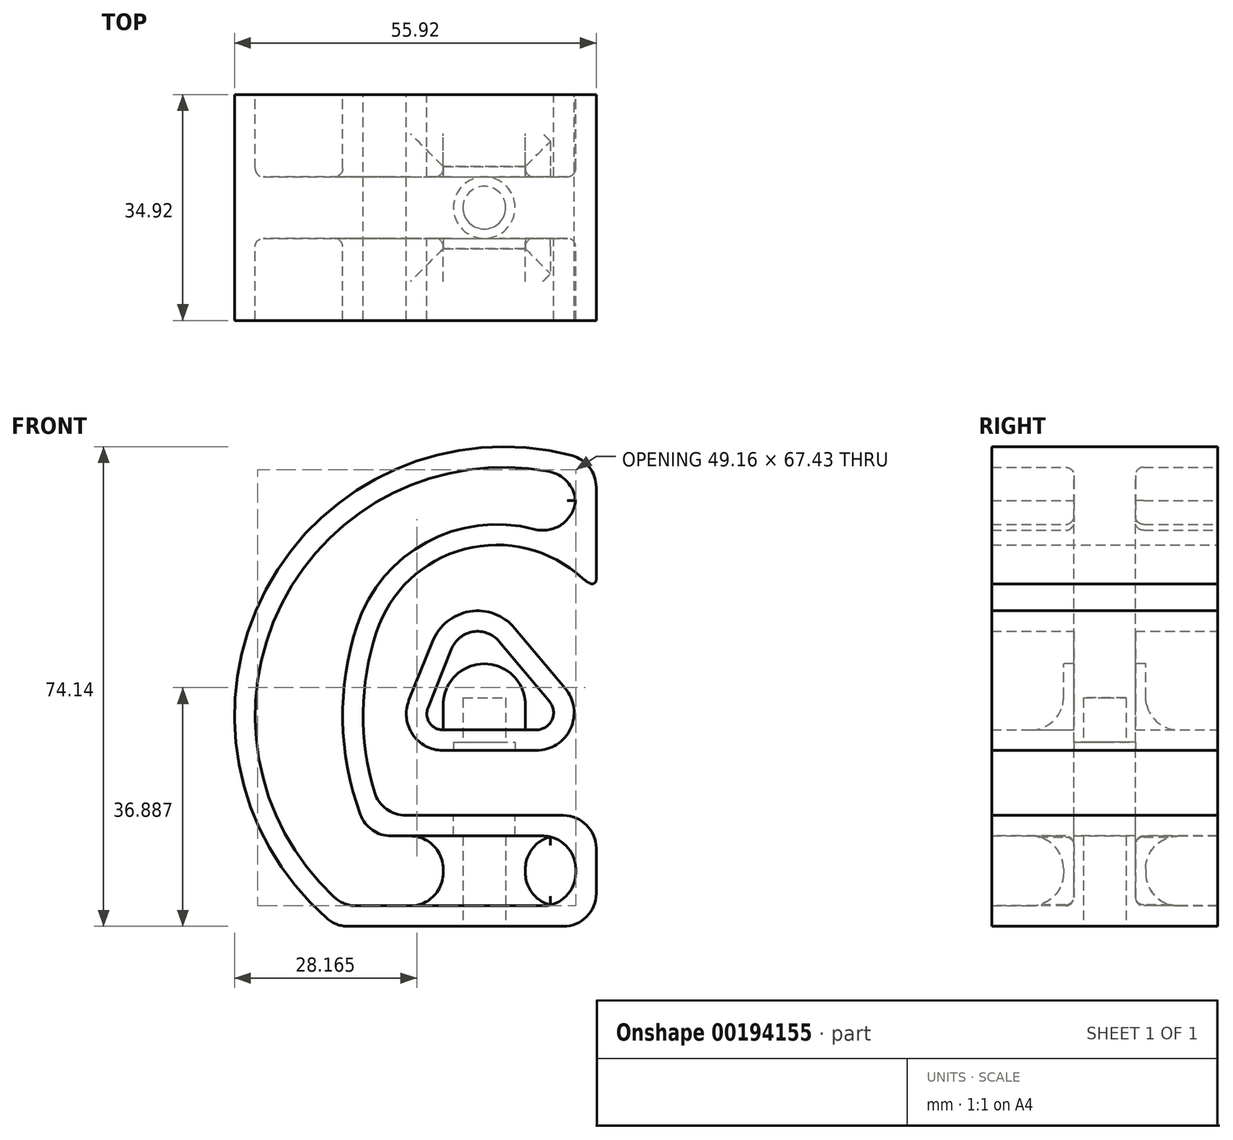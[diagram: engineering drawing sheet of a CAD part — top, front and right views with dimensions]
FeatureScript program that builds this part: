
annotation { "Feature Type Name" : "Feature", "Feature Type Description" : "" }
export const myFeature = defineFeature(function(context is Context, id is Id, definition is map)
    precondition{}
    {
        {
            var Q0;
            Q0=qCreatedBy(makeId("Front.planeOp"),FACE);
            var sketch = newSketch(context, id + "F0", { "sketchPlane" : qUnion([Q0])});
            skLineSegment(sketch, "E0", {"start": v(244.88, -10.5) * mm, "end": v(230.41, -10.5) * mm});
            skLineSegment(sketch, "E1", {"start": v(225.18, -2.77) * mm, "end": v(228.83, 6.36) * mm});
            skLineSegment(sketch, "E2", {"start": v(241.53, 8.4) * mm, "end": v(249.35, -0.9) * mm});
            skPoint(sketch, "E3.visualSharp", {"position": v(249.43, -10.5) * mm});
            skArc(sketch, "E3.filletArc", {"start": v(244.88, -10.5) * mm, "mid": v(250.17, -7.12) * mm, "end": v(249.35, -0.9) * mm});
            skArc(sketch, "E4", {"start": v(241.53, 8.4) * mm, "mid": v(234.6, 10.98) * mm, "end": v(228.83, 6.36) * mm});
            skArc(sketch, "E5", {"start": v(225.18, -2.77) * mm, "mid": v(225.74, -8.02) * mm, "end": v(230.41, -10.5) * mm});
            skPoint(sketch, "E6.visualSharp", {"position": v(249.72, -1.34) * mm});
            skLineSegment(sketch, "E7", {"start": v(254.14, 33.9) * mm, "end": v(254.14, 14.98) * mm});
            skLineSegment(sketch, "E8", {"start": v(254.14, 14.98) * mm, "end": v(253.16, 14.98) * mm});
            skLineSegment(sketch, "E9", {"start": v(213.99, -37.7) * mm, "end": v(254.14, -37.7) * mm});
            skLineSegment(sketch, "E10", {"start": v(254.14, -37.7) * mm, "end": v(254.14, -20.55) * mm});
            skLineSegment(sketch, "E11", {"start": v(254.14, -20.55) * mm, "end": v(221.13, -20.55) * mm});
            skArc(sketch, "E12", {"start": v(220.15, 7.77) * mm, "mid": v(218.13, -6.48) * mm, "end": v(221.13, -20.55) * mm});
            skArc(sketch, "E13", {"start": v(254.14, 33.9) * mm, "mid": v(203.53, 15.22) * mm, "end": v(213.99, -37.7) * mm});
            skArc(sketch, "E14", {"start": v(253.16, 14.98) * mm, "mid": v(234.6, 20.81) * mm, "end": v(220.15, 7.77) * mm});
            skLineSegment(sketch, "E15.0", {"start": v(239.1, 6.36) * mm, "end": v(246.92, -2.94) * mm});
            skLineSegment(sketch, "E15.1", {"start": v(228.13, -3.95) * mm, "end": v(231.78, 5.18) * mm});
            skArc(sketch, "E15.2", {"start": v(228.13, -3.95) * mm, "mid": v(228.37, -6.24) * mm, "end": v(230.41, -7.32) * mm});
            skArc(sketch, "E15.3", {"start": v(239.1, 6.36) * mm, "mid": v(235.1, 7.85) * mm, "end": v(231.78, 5.18) * mm});
            skLineSegment(sketch, "E15.4", {"start": v(244.88, -7.32) * mm, "end": v(230.41, -7.32) * mm});
            skArc(sketch, "E15.5", {"start": v(244.88, -7.32) * mm, "mid": v(247.3, -5.78) * mm, "end": v(246.92, -2.94) * mm});
            skLineSegment(sketch, "E16.0", {"start": v(250.96, 31.6) * mm, "end": v(250.96, 20.9) * mm});
            skArc(sketch, "E16.2", {"start": v(250.96, 31.6) * mm, "mid": v(206.04, 13.18) * mm, "end": v(215.12, -34.52) * mm});
            skArc(sketch, "E16.4", {"start": v(250.96, 20.9) * mm, "mid": v(231.08, 23.1) * mm, "end": v(217.13, 8.76) * mm});
            skLineSegment(sketch, "E16.5", {"start": v(215.12, -34.52) * mm, "end": v(250.96, -34.52) * mm});
            skLineSegment(sketch, "E16.6", {"start": v(250.96, -34.52) * mm, "end": v(250.96, -23.72) * mm});
            skLineSegment(sketch, "E16.7", {"start": v(250.96, -23.72) * mm, "end": v(219.05, -23.72) * mm});
            skArc(sketch, "E16.8", {"start": v(217.13, 8.76) * mm, "mid": v(215, -7.67) * mm, "end": v(219.05, -23.72) * mm});
            skSolve(sketch);
        }
        {
            var Q0;
            Q0 = qSketchRegion(id + "F0", true);
            extrude(context, id + "F1", {"entities" : qUnion([Q0]), "depth" : 34.92 * mm});
        }
        {
            var Q0;
            Q0=makeQuery(id+"F1.opExtrude","SWEPT_EDGE",EDGE,{"disambiguationData":[OSD([sQuery(id+"F0.wireOp",EDGE,"E11"),sQuery(id+"F0.wireOp",EDGE,"E12")])]});
            fillet(context, id + "F2", {"entities" : qUnion([Q0]), "radius" : 5.08 * mm, "tangentPropagation" : true, "allowEdgeOverflow" : false});
        }
        {
            var Q0;
            Q0=makeQuery(id+"F1.opExtrude","SWEPT_EDGE",EDGE,{"disambiguationData":[OSD([sQuery(id+"F0.wireOp",EDGE,"E14"),sQuery(id+"F0.wireOp",EDGE,"j8sf52jT-AdPT-Hs1F-RymM-NBzSZyB4l8sF")])]});
            fillet(context, id + "F3", {"entities" : qUnion([Q0]), "radius" : 5.08 * mm, "tangentPropagation" : true, "allowEdgeOverflow" : false});
        }
        {
            var Q0;
            Q0=makeQuery(id+"F1.opExtrude","SWEPT_EDGE",EDGE,{"disambiguationData":[OSD([sQuery(id+"F0.wireOp",EDGE,"E7"),sQuery(id+"F0.wireOp",EDGE,"E13")])]});
            fillet(context, id + "F4", {"entities" : qUnion([Q0]), "radius" : 5.08 * mm, "tangentPropagation" : true, "allowEdgeOverflow" : false});
        }
        {
            var Q0;
            Q0=qCreatedBy(makeId("Front.planeOp"),FACE);
            cPlane(context, id + "F5", {"entities" : qUnion([Q0]), "cplaneType" : CPlaneType.OFFSET, "offset" : 17.46 * mm, "width" : 152.4 * mm, "height" : 152.4 * mm});
        }
        {
            var Q0;
            Q0=makeQuery(id+"F1.opExtrude","SWEPT_EDGE",EDGE,{"disambiguationData":[OSD([sQuery(id+"F0.wireOp",EDGE,"E7"),sQuery(id+"F0.wireOp",EDGE,"E8")])]});
            var Q1;
            Q1=makeQuery(id+"F1.opExtrude","SWEPT_EDGE",EDGE,{"disambiguationData":[OSD([sQuery(id+"F0.wireOp",EDGE,"E10"),sQuery(id+"F0.wireOp",EDGE,"E11")])]});
            var Q2;
            Q2=makeQuery(id+"F1.opExtrude","SWEPT_EDGE",EDGE,{"disambiguationData":[OSD([sQuery(id+"F0.wireOp",EDGE,"E9"),sQuery(id+"F0.wireOp",EDGE,"E13")])]});
            fillet(context, id + "F6", {"entities" : qUnion([Q0, Q1, Q2]), "radius" : 5.08 * mm, "tangentPropagation" : true, "allowEdgeOverflow" : false});
        }
        {
            var Q0;
            Q0=qCreatedBy(makeId("Right.planeOp"),FACE);
            var sketch = newSketch(context, id + "F7", { "sketchPlane" : qUnion([Q0])});
            skLineSegment(sketch, "E17.bottom", {"start": v(-12.7, 42.6) * mm, "end": v(-22.22, 42.6) * mm});
            skLineSegment(sketch, "E17.top", {"start": v(-12.7, -42.6) * mm, "end": v(-22.23, -42.6) * mm});
            skLineSegment(sketch, "E17.left", {"start": v(-12.7, 42.6) * mm, "end": v(-12.7, -42.6) * mm});
            skLineSegment(sketch, "E17.right", {"start": v(-22.22, 42.6) * mm, "end": v(-22.23, -42.6) * mm});
            skPoint(sketch, "E17.middle", {"position": v(-17.46, 0) * mm});
            skSolve(sketch);
        }
        {
            var Q0;
            Q0 = qSketchRegion(id + "F7", true);
            extrude(context, id + "F8", {"entities" : qUnion([Q0]), "depth" : 308.6 * mm});
        }
        {
            var Q0;
            Q0=makeQuery(id+"F1.opExtrude","SWEPT_BODY",BODY,{"disambiguationData":[OSD([sQuery(id+"F0.wireOp",EDGE,"E7"),sQuery(id+"F0.wireOp",EDGE,"E8"),sQuery(id+"F0.wireOp",EDGE,"E9"),sQuery(id+"F0.wireOp",EDGE,"E10"),sQuery(id+"F0.wireOp",EDGE,"E11"),sQuery(id+"F0.wireOp",EDGE,"E12"),sQuery(id+"F0.wireOp",EDGE,"E13"),sQuery(id+"F0.wireOp",EDGE,"E14"),sQuery(id+"F0.wireOp",EDGE,"j8sf52jT-AdPT-Hs1F-RymM-NBzSZyB4l8sF"),sQuery(id+"F0.wireOp",EDGE,"E16.0"),sQuery(id+"F0.wireOp",EDGE,"E16.1"),sQuery(id+"F0.wireOp",EDGE,"E16.2"),sQuery(id+"F0.wireOp",EDGE,"E16.3"),sQuery(id+"F0.wireOp",EDGE,"E16.4"),sQuery(id+"F0.wireOp",EDGE,"E16.5"),sQuery(id+"F0.wireOp",EDGE,"E16.6"),sQuery(id+"F0.wireOp",EDGE,"E16.7"),sQuery(id+"F0.wireOp",EDGE,"E16.8")])]});
            var Q1;
            Q1=makeQuery(id+"F1.opExtrude","SWEPT_BODY",BODY,{"disambiguationData":[OSD([sQuery(id+"F0.wireOp",EDGE,"E0"),sQuery(id+"F0.wireOp",EDGE,"E1"),sQuery(id+"F0.wireOp",EDGE,"E2"),sQuery(id+"F0.wireOp",EDGE,"E3.filletArc"),sQuery(id+"F0.wireOp",EDGE,"E4"),sQuery(id+"F0.wireOp",EDGE,"E5"),sQuery(id+"F0.wireOp",EDGE,"E15.0"),sQuery(id+"F0.wireOp",EDGE,"E15.1"),sQuery(id+"F0.wireOp",EDGE,"E15.2"),sQuery(id+"F0.wireOp",EDGE,"E15.3"),sQuery(id+"F0.wireOp",EDGE,"E15.4"),sQuery(id+"F0.wireOp",EDGE,"E15.5")])]});
            var Q2;
            Q2=makeQuery(id+"F8.opExtrude","SWEPT_BODY",BODY,{"disambiguationData":[OSD([sQuery(id+"F7.wireOp",EDGE,"E17.bottom"),sQuery(id+"F7.wireOp",EDGE,"E17.top"),sQuery(id+"F7.wireOp",EDGE,"E17.left"),sQuery(id+"F7.wireOp",EDGE,"E17.right")])]});
            booleanBodies(context, id + "F9", {"operationType" : BooleanOperationType.UNION, "tools" : qUnion([Q0, Q1, Q2]), "keepTools" : true});
        }
        {
            var Q0;
            Q0=makeQuery(id+"F1.opExtrude","CAP_FACE",FACE,{"disambiguationData":[OSD([sQuery(id+"F0.wireOp",EDGE,"E7"),sQuery(id+"F0.wireOp",EDGE,"E8"),sQuery(id+"F0.wireOp",EDGE,"E9"),sQuery(id+"F0.wireOp",EDGE,"E10"),sQuery(id+"F0.wireOp",EDGE,"E11"),sQuery(id+"F0.wireOp",EDGE,"E12"),sQuery(id+"F0.wireOp",EDGE,"E13"),sQuery(id+"F0.wireOp",EDGE,"E14"),sQuery(id+"F0.wireOp",EDGE,"j8sf52jT-AdPT-Hs1F-RymM-NBzSZyB4l8sF"),sQuery(id+"F0.wireOp",EDGE,"E16.0"),sQuery(id+"F0.wireOp",EDGE,"E16.1"),sQuery(id+"F0.wireOp",EDGE,"E16.2"),sQuery(id+"F0.wireOp",EDGE,"E16.3"),sQuery(id+"F0.wireOp",EDGE,"E16.4"),sQuery(id+"F0.wireOp",EDGE,"E16.5"),sQuery(id+"F0.wireOp",EDGE,"E16.6"),sQuery(id+"F0.wireOp",EDGE,"E16.7"),sQuery(id+"F0.wireOp",EDGE,"E16.8")])],"isStart":false});
            var sketch = newSketch(context, id + "F10", { "sketchPlane" : qUnion([Q0])});
            skArc(sketch, "E18.0", {"start": v(251.99, 16.14) * mm, "mid": v(233.79, 20.62) * mm, "end": v(220.15, 7.77) * mm});
            skArc(sketch, "E18.1", {"start": v(220.15, 7.77) * mm, "mid": v(218.1, -4.56) * mm, "end": v(219.85, -16.93) * mm});
            skArc(sketch, "E18.2", {"start": v(224.72, -20.55) * mm, "mid": v(221.69, -19.55) * mm, "end": v(219.85, -16.93) * mm});
            skLineSegment(sketch, "E18.3", {"start": v(249.06, -20.55) * mm, "end": v(224.72, -20.55) * mm});
            skArc(sketch, "E18.4", {"start": v(254.14, -25.63) * mm, "mid": v(252.65, -22.04) * mm, "end": v(249.06, -20.55) * mm});
            skLineSegment(sketch, "E18.5", {"start": v(254.14, -37.7) * mm, "end": v(254.14, -25.63) * mm});
            skLineSegment(sketch, "E18.6", {"start": v(215.82, -37.7) * mm, "end": v(254.14, -37.7) * mm});
            skArc(sketch, "E18.7", {"start": v(250.35, 35.08) * mm, "mid": v(203.05, 14.34) * mm, "end": v(212.49, -36.45) * mm});
            skArc(sketch, "E18.8", {"start": v(254.14, 30.17) * mm, "mid": v(253.08, 33.27) * mm, "end": v(250.35, 35.08) * mm});
            skArc(sketch, "E19.0", {"start": v(241.53, 8.4) * mm, "mid": v(234.6, 10.98) * mm, "end": v(228.83, 6.36) * mm});
            skLineSegment(sketch, "E19.1", {"start": v(241.53, 8.4) * mm, "end": v(249.35, -0.9) * mm});
            skArc(sketch, "E19.2", {"start": v(244.88, -10.5) * mm, "mid": v(250.17, -7.12) * mm, "end": v(249.35, -0.9) * mm});
            skLineSegment(sketch, "E19.3", {"start": v(244.88, -10.5) * mm, "end": v(230.41, -10.5) * mm});
            skLineSegment(sketch, "E19.4", {"start": v(225.18, -2.77) * mm, "end": v(228.83, 6.36) * mm});
            skArc(sketch, "E19.5", {"start": v(225.18, -2.77) * mm, "mid": v(225.74, -8.02) * mm, "end": v(230.41, -10.5) * mm});
            skLineSegment(sketch, "E20.0", {"start": v(308.6, 42.6) * mm, "end": v(0, 42.6) * mm});
            skLineSegment(sketch, "E20.1", {"start": v(308.6, 42.6) * mm, "end": v(308.6, -42.6) * mm});
            skLineSegment(sketch, "E20.2", {"start": v(308.6, -42.6) * mm, "end": v(0, -42.6) * mm});
            skLineSegment(sketch, "E21.0", {"start": v(0, 42.6) * mm, "end": v(0, -42.6) * mm});
            skArc(sketch, "E22.0", {"start": v(212.49, -36.45) * mm, "mid": v(214.04, -37.37) * mm, "end": v(215.82, -37.7) * mm});
            skLineSegment(sketch, "E23.0", {"start": v(254.14, 30.17) * mm, "end": v(254.14, 14.98) * mm});
            skArc(sketch, "E23.1", {"start": v(251.99, 16.14) * mm, "mid": v(253, 15.43) * mm, "end": v(254.14, 14.98) * mm});
            skSolve(sketch);
        }
        {
            var Q0;
            Q0 = qSketchRegion(id + "F10", true);
            extrude(context, id + "F11", {"entities" : qUnion([Q0]), "operationType" : NewBodyOperationType.REMOVE, "oppositeDirection" : true, "depth" : 47.5 * mm});
        }
        {
            var Q0;
            Q0=qCreatedBy(id+"F5.planeOp",FACE);
            var sketch = newSketch(context, id + "F12", { "sketchPlane" : qUnion([Q0])});
            skLineSegment(sketch, "E24.top", {"start": v(230.48, -37.7) * mm, "end": v(243.18, -37.7) * mm});
            skLineSegment(sketch, "E24.left", {"start": v(230.48, -20.55) * mm, "end": v(230.48, -37.7) * mm});
            skLineSegment(sketch, "E24.right", {"start": v(243.18, -20.55) * mm, "end": v(243.18, -37.7) * mm});
            skLineSegment(sketch, "E25.bottom", {"start": v(230.48, -9.16) * mm, "end": v(243.18, -9.16) * mm});
            skLineSegment(sketch, "E25.left", {"start": v(230.48, -9.16) * mm, "end": v(230.48, -3.46) * mm});
            skLineSegment(sketch, "E25.right", {"start": v(243.18, -9.16) * mm, "end": v(243.18, -3.46) * mm});
            skArc(sketch, "E26", {"start": v(243.18, -3.46) * mm, "mid": v(236.83, 2.89) * mm, "end": v(230.48, -3.46) * mm});
            skLineSegment(sketch, "E27", {"start": v(236.83, -3.46) * mm, "end": v(236.83, -20.58) * mm, "construction": true});
            skLineSegment(sketch, "E28", {"start": v(230.48, -20.55) * mm, "end": v(243.18, -20.55) * mm});
            skSolve(sketch);
        }
        {
            var Q0;
            Q0 = qSketchRegion(id + "F12", true);
            extrude(context, id + "F13", {"entities" : qUnion([Q0]), "oppositeDirection" : true, "depth" : 6.35 * mm, "hasSecondDirection" : true, "secondDirectionOppositeDirection" : false, "secondDirectionDepth" : 6.35 * mm});
        }
        {
            var Q0;
            Q0=makeQuery(id+"F11.boolean.opBoolean","SPLIT",BODY,{"disambiguationData":[OD(1.0)],"derivedFrom":makeQuery(id+"F1.opExtrude","SWEPT_BODY",BODY,{"disambiguationData":[OSD([sQuery(id+"F0.wireOp",EDGE,"E7"),sQuery(id+"F0.wireOp",EDGE,"E8"),sQuery(id+"F0.wireOp",EDGE,"E9"),sQuery(id+"F0.wireOp",EDGE,"E10"),sQuery(id+"F0.wireOp",EDGE,"E11"),sQuery(id+"F0.wireOp",EDGE,"E12"),sQuery(id+"F0.wireOp",EDGE,"E13"),sQuery(id+"F0.wireOp",EDGE,"E14"),sQuery(id+"F0.wireOp",EDGE,"j8sf52jT-AdPT-Hs1F-RymM-NBzSZyB4l8sF"),sQuery(id+"F0.wireOp",EDGE,"E16.0"),sQuery(id+"F0.wireOp",EDGE,"E16.1"),sQuery(id+"F0.wireOp",EDGE,"E16.2"),sQuery(id+"F0.wireOp",EDGE,"E16.3"),sQuery(id+"F0.wireOp",EDGE,"E16.4"),sQuery(id+"F0.wireOp",EDGE,"E16.5"),sQuery(id+"F0.wireOp",EDGE,"E16.6"),sQuery(id+"F0.wireOp",EDGE,"E16.7"),sQuery(id+"F0.wireOp",EDGE,"E16.8")])]})});
            var Q1;
            Q1=makeQuery(id+"F13.opExtrude","SWEPT_BODY",BODY,{"disambiguationData":[OSD([sQuery(id+"F12.wireOp",EDGE,"E24.top"),sQuery(id+"F12.wireOp",EDGE,"E24.left"),sQuery(id+"F12.wireOp",EDGE,"E24.right"),sQuery(id+"F12.wireOp",EDGE,"E28")])]});
            booleanBodies(context, id + "F14", {"operationType" : BooleanOperationType.UNION, "tools" : qUnion([Q0, Q1])});
        }
        {
            var Q0;
            Q0=makeQuery(id+"F13.opExtrude","SWEPT_BODY",BODY,{"disambiguationData":[OSD([sQuery(id+"F12.wireOp",EDGE,"E25.bottom"),sQuery(id+"F12.wireOp",EDGE,"E25.left"),sQuery(id+"F12.wireOp",EDGE,"E25.right"),sQuery(id+"F12.wireOp",EDGE,"E26")])]});
            var Q1;
            Q1=makeQuery(id+"F11.boolean.opBoolean","SPLIT",BODY,{"disambiguationData":[OD(0.0)],"derivedFrom":makeQuery(id+"F1.opExtrude","SWEPT_BODY",BODY,{"disambiguationData":[OSD([sQuery(id+"F0.wireOp",EDGE,"E7"),sQuery(id+"F0.wireOp",EDGE,"E8"),sQuery(id+"F0.wireOp",EDGE,"E9"),sQuery(id+"F0.wireOp",EDGE,"E10"),sQuery(id+"F0.wireOp",EDGE,"E11"),sQuery(id+"F0.wireOp",EDGE,"E12"),sQuery(id+"F0.wireOp",EDGE,"E13"),sQuery(id+"F0.wireOp",EDGE,"E14"),sQuery(id+"F0.wireOp",EDGE,"j8sf52jT-AdPT-Hs1F-RymM-NBzSZyB4l8sF"),sQuery(id+"F0.wireOp",EDGE,"E16.0"),sQuery(id+"F0.wireOp",EDGE,"E16.1"),sQuery(id+"F0.wireOp",EDGE,"E16.2"),sQuery(id+"F0.wireOp",EDGE,"E16.3"),sQuery(id+"F0.wireOp",EDGE,"E16.4"),sQuery(id+"F0.wireOp",EDGE,"E16.5"),sQuery(id+"F0.wireOp",EDGE,"E16.6"),sQuery(id+"F0.wireOp",EDGE,"E16.7"),sQuery(id+"F0.wireOp",EDGE,"E16.8")])]})});
            booleanBodies(context, id + "F15", {"operationType" : BooleanOperationType.UNION, "tools" : qUnion([Q0, Q1])});
        }
        {
            var Q0;
            {var subQ1=sQuery(id+"F0.wireOp",EDGE,"E16.7");Q0=makeQuery(id+"F14.opBoolean","INTERSECT",EDGE,{"derivedFrom":[makeQuery(id+"F9.opBoolean","SPLIT",FACE,{"disambiguationData":[TD([makeQuery(id+"F8.opExtrude","SWEPT_FACE",FACE,{"disambiguationData":[OSD([sQuery(id+"F7.wireOp",EDGE,"E17.right")])]})])],"derivedFrom":makeQuery(id+"F1.opExtrude","SWEPT_FACE",FACE,{"disambiguationData":[OSD([subQ1])]})}),makeQuery(id+"F13.opExtrude","CAP_FACE",FACE,{"disambiguationData":[OSD([sQuery(id+"F12.wireOp",EDGE,"E24.top"),sQuery(id+"F12.wireOp",EDGE,"E24.left"),sQuery(id+"F12.wireOp",EDGE,"E24.right"),sQuery(id+"F12.wireOp",EDGE,"E28")])],"isStart":true})]});}
            var Q1;
            {var subQ1=sQuery(id+"F0.wireOp",EDGE,"E16.5");Q1=makeQuery(id+"F14.opBoolean","INTERSECT",EDGE,{"derivedFrom":[makeQuery(id+"F9.opBoolean","SPLIT",FACE,{"disambiguationData":[TD([makeQuery(id+"F8.opExtrude","SWEPT_FACE",FACE,{"disambiguationData":[OSD([sQuery(id+"F7.wireOp",EDGE,"E17.right")])]})])],"derivedFrom":makeQuery(id+"F1.opExtrude","SWEPT_FACE",FACE,{"disambiguationData":[OSD([subQ1])]})}),makeQuery(id+"F13.opExtrude","CAP_FACE",FACE,{"disambiguationData":[OSD([sQuery(id+"F12.wireOp",EDGE,"E24.top"),sQuery(id+"F12.wireOp",EDGE,"E24.left"),sQuery(id+"F12.wireOp",EDGE,"E24.right"),sQuery(id+"F12.wireOp",EDGE,"E28")])],"isStart":true})]});}
            var Q2;
            {var subQ1=sQuery(id+"F0.wireOp",EDGE,"E15.4");Q2=makeQuery(id+"F15.opBoolean","INTERSECT",EDGE,{"derivedFrom":[makeQuery(id+"F9.opBoolean","SPLIT",FACE,{"disambiguationData":[TD([makeQuery(id+"F8.opExtrude","SWEPT_FACE",FACE,{"disambiguationData":[OSD([sQuery(id+"F7.wireOp",EDGE,"E17.right")])]})])],"derivedFrom":makeQuery(id+"F1.opExtrude","SWEPT_FACE",FACE,{"disambiguationData":[OSD([subQ1])]})}),makeQuery(id+"F13.opExtrude","CAP_FACE",FACE,{"disambiguationData":[OSD([sQuery(id+"F12.wireOp",EDGE,"E25.bottom"),sQuery(id+"F12.wireOp",EDGE,"E25.left"),sQuery(id+"F12.wireOp",EDGE,"E25.right"),sQuery(id+"F12.wireOp",EDGE,"E26")])],"isStart":true})]});}
            var Q3;
            {var subQ1=sQuery(id+"F0.wireOp",EDGE,"E16.5");Q3=makeQuery(id+"F14.opBoolean","INTERSECT",EDGE,{"derivedFrom":[makeQuery(id+"F9.opBoolean","SPLIT",FACE,{"disambiguationData":[TD([makeQuery(id+"F8.opExtrude","SWEPT_FACE",FACE,{"disambiguationData":[OSD([sQuery(id+"F7.wireOp",EDGE,"E17.left")])]})])],"derivedFrom":makeQuery(id+"F1.opExtrude","SWEPT_FACE",FACE,{"disambiguationData":[OSD([subQ1])]})}),makeQuery(id+"F13.opExtrude","CAP_FACE",FACE,{"disambiguationData":[OSD([sQuery(id+"F12.wireOp",EDGE,"E24.top"),sQuery(id+"F12.wireOp",EDGE,"E24.left"),sQuery(id+"F12.wireOp",EDGE,"E24.right"),sQuery(id+"F12.wireOp",EDGE,"E28")])],"isStart":false})]});}
            var Q4;
            {var subQ1=sQuery(id+"F0.wireOp",EDGE,"E15.4");Q4=makeQuery(id+"F15.opBoolean","INTERSECT",EDGE,{"derivedFrom":[makeQuery(id+"F9.opBoolean","SPLIT",FACE,{"disambiguationData":[TD([makeQuery(id+"F8.opExtrude","SWEPT_FACE",FACE,{"disambiguationData":[OSD([sQuery(id+"F7.wireOp",EDGE,"E17.left")])]})])],"derivedFrom":makeQuery(id+"F1.opExtrude","SWEPT_FACE",FACE,{"disambiguationData":[OSD([subQ1])]})}),makeQuery(id+"F13.opExtrude","CAP_FACE",FACE,{"disambiguationData":[OSD([sQuery(id+"F12.wireOp",EDGE,"E25.bottom"),sQuery(id+"F12.wireOp",EDGE,"E25.left"),sQuery(id+"F12.wireOp",EDGE,"E25.right"),sQuery(id+"F12.wireOp",EDGE,"E26")])],"isStart":false})]});}
            var Q5;
            {var subQ1=sQuery(id+"F0.wireOp",EDGE,"E16.7");Q5=makeQuery(id+"F14.opBoolean","INTERSECT",EDGE,{"derivedFrom":[makeQuery(id+"F9.opBoolean","SPLIT",FACE,{"disambiguationData":[TD([makeQuery(id+"F8.opExtrude","SWEPT_FACE",FACE,{"disambiguationData":[OSD([sQuery(id+"F7.wireOp",EDGE,"E17.left")])]})])],"derivedFrom":makeQuery(id+"F1.opExtrude","SWEPT_FACE",FACE,{"disambiguationData":[OSD([subQ1])]})}),makeQuery(id+"F13.opExtrude","CAP_FACE",FACE,{"disambiguationData":[OSD([sQuery(id+"F12.wireOp",EDGE,"E24.top"),sQuery(id+"F12.wireOp",EDGE,"E24.left"),sQuery(id+"F12.wireOp",EDGE,"E24.right"),sQuery(id+"F12.wireOp",EDGE,"E28")])],"isStart":false})]});}
            fillet(context, id + "F16", {"entities" : qUnion([Q0, Q1, Q2, Q3, Q4, Q5]), "radius" : 5.08 * mm, "tangentPropagation" : true, "allowEdgeOverflow" : false});
        }
        {
            var Q0;
            {var subQ0=sQuery(id+"F0.wireOp",EDGE,"E16.8");var subQ1=sQuery(id+"F0.wireOp",EDGE,"E16.7");Q0=makeQuery(id+"F9.opBoolean","SPLIT",EDGE,{"disambiguationData":[TD([makeQuery(id+"F8.opExtrude","SWEPT_FACE",FACE,{"disambiguationData":[OSD([sQuery(id+"F7.wireOp",EDGE,"E17.right")])]})])],"derivedFrom":makeQuery(id+"F1.opExtrude","SWEPT_EDGE",EDGE,{"disambiguationData":[OSD([subQ1,subQ0])]})});}
            var Q1;
            {var subQ0=sQuery(id+"F0.wireOp",EDGE,"E16.8");var subQ1=sQuery(id+"F0.wireOp",EDGE,"E16.7");Q1=makeQuery(id+"F9.opBoolean","SPLIT",EDGE,{"disambiguationData":[TD([makeQuery(id+"F8.opExtrude","SWEPT_FACE",FACE,{"disambiguationData":[OSD([sQuery(id+"F7.wireOp",EDGE,"E17.left")])]})])],"derivedFrom":makeQuery(id+"F1.opExtrude","SWEPT_EDGE",EDGE,{"disambiguationData":[OSD([subQ1,subQ0])]})});}
            fillet(context, id + "F17", {"entities" : qUnion([Q0, Q1]), "radius" : 5.08 * mm, "tangentPropagation" : true, "allowEdgeOverflow" : false});
        }
        {
            var Q0;
            {var subQ15=sQuery(id+"F0.wireOp",EDGE,"E9");var subQ20=makeQuery(id+"F1.opExtrude","SWEPT_FACE",FACE,{"disambiguationData":[OSD([subQ15])]});Q0=makeQuery(id+"F11.boolean.opBoolean","MERGE",FACE,{"derivedFrom":[makeQuery(id+"F9.opBoolean","SPLIT",FACE,{"disambiguationData":[TD([makeQuery(id+"F8.opExtrude","SWEPT_FACE",FACE,{"disambiguationData":[OSD([sQuery(id+"F7.wireOp",EDGE,"E17.left")])]})])],"derivedFrom":subQ20}),makeQuery(id+"F9.opBoolean","SPLIT",FACE,{"disambiguationData":[TD([makeQuery(id+"F8.opExtrude","SWEPT_FACE",FACE,{"disambiguationData":[OSD([sQuery(id+"F7.wireOp",EDGE,"E17.right")])]})])],"derivedFrom":subQ20}),makeQuery(id+"F11.opExtrude","SWEPT_FACE",FACE,{"disambiguationData":[OSD([sQuery(id+"F10.wireOp",EDGE,"E18.6")])]})]});}
            var sketch = newSketch(context, id + "F18", { "sketchPlane" : qUnion([Q0])});
            skLineSegment(sketch, "E29", {"start": v(254.14, 17.46) * mm, "end": v(196.23, 17.46) * mm, "construction": true});
            skPoint(sketch, "E30.0", {"position": v(236.83, 11.11) * mm});
            skCircle(sketch, "E31", {"center": v(236.83, 17.46) * mm, "radius": 3.3 * mm});
            skSolve(sketch);
        }
        {
            var Q0;
            Q0 = qSketchRegion(id + "F18", true);
            extrude(context, id + "F19", {"entities" : qUnion([Q0]), "operationType" : NewBodyOperationType.REMOVE, "oppositeDirection" : true, "depth" : 35.3 * mm});
        }
        {
            var Q0;
            {var subQ13=sQuery(id+"F0.wireOp",EDGE,"E11");var subQ20=makeQuery(id+"F1.opExtrude","SWEPT_FACE",FACE,{"disambiguationData":[OSD([subQ13])]});Q0=makeQuery(id+"F11.boolean.opBoolean","MERGE",FACE,{"derivedFrom":[makeQuery(id+"F9.opBoolean","SPLIT",FACE,{"disambiguationData":[TD([makeQuery(id+"F8.opExtrude","SWEPT_FACE",FACE,{"disambiguationData":[OSD([sQuery(id+"F7.wireOp",EDGE,"E17.left")])]})])],"derivedFrom":subQ20}),makeQuery(id+"F9.opBoolean","SPLIT",FACE,{"disambiguationData":[TD([makeQuery(id+"F8.opExtrude","SWEPT_FACE",FACE,{"disambiguationData":[OSD([sQuery(id+"F7.wireOp",EDGE,"E17.right")])]})])],"derivedFrom":subQ20}),makeQuery(id+"F11.opExtrude","SWEPT_FACE",FACE,{"disambiguationData":[OSD([sQuery(id+"F10.wireOp",EDGE,"E18.3")])]})]});}
            var sketch = newSketch(context, id + "F20", { "sketchPlane" : qUnion([Q0])});
            skCircle(sketch, "E32", {"center": v(236.83, -17.46) * mm, "radius": 4.76 * mm});
            skSolve(sketch);
        }
        {
            var Q0;
            Q0 = qSketchRegion(id + "F20", true);
            extrude(context, id + "F21", {"entities" : qUnion([Q0]), "operationType" : NewBodyOperationType.REMOVE, "oppositeDirection" : true, "depth" : 3.17 * mm});
        }
        {
            var Q0;
            {var subQ0=sQuery(id+"F0.wireOp",EDGE,"E16.7");var subQ1=sQuery(id+"F0.wireOp",EDGE,"E16.6");Q0=makeQuery(id+"F9.opBoolean","SPLIT",EDGE,{"disambiguationData":[TD([makeQuery(id+"F8.opExtrude","SWEPT_FACE",FACE,{"disambiguationData":[OSD([sQuery(id+"F7.wireOp",EDGE,"E17.left")])]})])],"derivedFrom":makeQuery(id+"F1.opExtrude","SWEPT_EDGE",EDGE,{"disambiguationData":[OSD([subQ1,subQ0])]})});}
            var Q1;
            {var subQ1=sQuery(id+"F0.wireOp",EDGE,"E16.7");Q1=makeQuery(id+"F14.opBoolean","INTERSECT",EDGE,{"derivedFrom":[makeQuery(id+"F9.opBoolean","SPLIT",FACE,{"disambiguationData":[TD([makeQuery(id+"F8.opExtrude","SWEPT_FACE",FACE,{"disambiguationData":[OSD([sQuery(id+"F7.wireOp",EDGE,"E17.left")])]})])],"derivedFrom":makeQuery(id+"F1.opExtrude","SWEPT_FACE",FACE,{"disambiguationData":[OSD([subQ1])]})}),makeQuery(id+"F13.opExtrude","SWEPT_FACE",FACE,{"disambiguationData":[OSD([sQuery(id+"F12.wireOp",EDGE,"E24.right")])]})]});}
            var Q2;
            {var subQ0=sQuery(id+"F0.wireOp",EDGE,"E16.6");var subQ1=sQuery(id+"F0.wireOp",EDGE,"E16.5");Q2=makeQuery(id+"F9.opBoolean","SPLIT",EDGE,{"disambiguationData":[TD([makeQuery(id+"F8.opExtrude","SWEPT_FACE",FACE,{"disambiguationData":[OSD([sQuery(id+"F7.wireOp",EDGE,"E17.left")])]})])],"derivedFrom":makeQuery(id+"F1.opExtrude","SWEPT_EDGE",EDGE,{"disambiguationData":[OSD([subQ1,subQ0])]})});}
            var Q3;
            {var subQ1=sQuery(id+"F0.wireOp",EDGE,"E16.5");Q3=makeQuery(id+"F14.opBoolean","INTERSECT",EDGE,{"derivedFrom":[makeQuery(id+"F9.opBoolean","SPLIT",FACE,{"disambiguationData":[TD([makeQuery(id+"F8.opExtrude","SWEPT_FACE",FACE,{"disambiguationData":[OSD([sQuery(id+"F7.wireOp",EDGE,"E17.left")])]})])],"derivedFrom":makeQuery(id+"F1.opExtrude","SWEPT_FACE",FACE,{"disambiguationData":[OSD([subQ1])]})}),makeQuery(id+"F13.opExtrude","SWEPT_FACE",FACE,{"disambiguationData":[OSD([sQuery(id+"F12.wireOp",EDGE,"E24.right")])]})]});}
            var Q4;
            {var subQ1=sQuery(id+"F0.wireOp",EDGE,"E16.7");Q4=makeQuery(id+"F14.opBoolean","INTERSECT",EDGE,{"derivedFrom":[makeQuery(id+"F9.opBoolean","SPLIT",FACE,{"disambiguationData":[TD([makeQuery(id+"F8.opExtrude","SWEPT_FACE",FACE,{"disambiguationData":[OSD([sQuery(id+"F7.wireOp",EDGE,"E17.left")])]})])],"derivedFrom":makeQuery(id+"F1.opExtrude","SWEPT_FACE",FACE,{"disambiguationData":[OSD([subQ1])]})}),makeQuery(id+"F13.opExtrude","SWEPT_FACE",FACE,{"disambiguationData":[OSD([sQuery(id+"F12.wireOp",EDGE,"E24.left")])]})]});}
            var Q5;
            {var subQ1=sQuery(id+"F0.wireOp",EDGE,"E16.5");Q5=makeQuery(id+"F14.opBoolean","INTERSECT",EDGE,{"derivedFrom":[makeQuery(id+"F9.opBoolean","SPLIT",FACE,{"disambiguationData":[TD([makeQuery(id+"F8.opExtrude","SWEPT_FACE",FACE,{"disambiguationData":[OSD([sQuery(id+"F7.wireOp",EDGE,"E17.left")])]})])],"derivedFrom":makeQuery(id+"F1.opExtrude","SWEPT_FACE",FACE,{"disambiguationData":[OSD([subQ1])]})}),makeQuery(id+"F13.opExtrude","SWEPT_FACE",FACE,{"disambiguationData":[OSD([sQuery(id+"F12.wireOp",EDGE,"E24.left")])]})]});}
            var Q6;
            {var subQ0=sQuery(id+"F0.wireOp",EDGE,"E16.6");var subQ1=sQuery(id+"F0.wireOp",EDGE,"E16.5");Q6=makeQuery(id+"F9.opBoolean","SPLIT",EDGE,{"disambiguationData":[TD([makeQuery(id+"F8.opExtrude","SWEPT_FACE",FACE,{"disambiguationData":[OSD([sQuery(id+"F7.wireOp",EDGE,"E17.right")])]})])],"derivedFrom":makeQuery(id+"F1.opExtrude","SWEPT_EDGE",EDGE,{"disambiguationData":[OSD([subQ1,subQ0])]})});}
            var Q7;
            {var subQ0=sQuery(id+"F0.wireOp",EDGE,"E16.7");var subQ1=sQuery(id+"F0.wireOp",EDGE,"E16.6");Q7=makeQuery(id+"F9.opBoolean","SPLIT",EDGE,{"disambiguationData":[TD([makeQuery(id+"F8.opExtrude","SWEPT_FACE",FACE,{"disambiguationData":[OSD([sQuery(id+"F7.wireOp",EDGE,"E17.right")])]})])],"derivedFrom":makeQuery(id+"F1.opExtrude","SWEPT_EDGE",EDGE,{"disambiguationData":[OSD([subQ1,subQ0])]})});}
            var Q8;
            {var subQ1=sQuery(id+"F0.wireOp",EDGE,"E16.7");Q8=makeQuery(id+"F14.opBoolean","INTERSECT",EDGE,{"derivedFrom":[makeQuery(id+"F9.opBoolean","SPLIT",FACE,{"disambiguationData":[TD([makeQuery(id+"F8.opExtrude","SWEPT_FACE",FACE,{"disambiguationData":[OSD([sQuery(id+"F7.wireOp",EDGE,"E17.right")])]})])],"derivedFrom":makeQuery(id+"F1.opExtrude","SWEPT_FACE",FACE,{"disambiguationData":[OSD([subQ1])]})}),makeQuery(id+"F13.opExtrude","SWEPT_FACE",FACE,{"disambiguationData":[OSD([sQuery(id+"F12.wireOp",EDGE,"E24.right")])]})]});}
            var Q9;
            {var subQ1=sQuery(id+"F0.wireOp",EDGE,"E16.5");Q9=makeQuery(id+"F14.opBoolean","INTERSECT",EDGE,{"derivedFrom":[makeQuery(id+"F9.opBoolean","SPLIT",FACE,{"disambiguationData":[TD([makeQuery(id+"F8.opExtrude","SWEPT_FACE",FACE,{"disambiguationData":[OSD([sQuery(id+"F7.wireOp",EDGE,"E17.right")])]})])],"derivedFrom":makeQuery(id+"F1.opExtrude","SWEPT_FACE",FACE,{"disambiguationData":[OSD([subQ1])]})}),makeQuery(id+"F13.opExtrude","SWEPT_FACE",FACE,{"disambiguationData":[OSD([sQuery(id+"F12.wireOp",EDGE,"E24.right")])]})]});}
            var Q10;
            {var subQ1=sQuery(id+"F0.wireOp",EDGE,"E16.5");Q10=makeQuery(id+"F14.opBoolean","INTERSECT",EDGE,{"derivedFrom":[makeQuery(id+"F9.opBoolean","SPLIT",FACE,{"disambiguationData":[TD([makeQuery(id+"F8.opExtrude","SWEPT_FACE",FACE,{"disambiguationData":[OSD([sQuery(id+"F7.wireOp",EDGE,"E17.right")])]})])],"derivedFrom":makeQuery(id+"F1.opExtrude","SWEPT_FACE",FACE,{"disambiguationData":[OSD([subQ1])]})}),makeQuery(id+"F13.opExtrude","SWEPT_FACE",FACE,{"disambiguationData":[OSD([sQuery(id+"F12.wireOp",EDGE,"E24.left")])]})]});}
            var Q11;
            {var subQ1=sQuery(id+"F0.wireOp",EDGE,"E16.7");Q11=makeQuery(id+"F14.opBoolean","INTERSECT",EDGE,{"derivedFrom":[makeQuery(id+"F9.opBoolean","SPLIT",FACE,{"disambiguationData":[TD([makeQuery(id+"F8.opExtrude","SWEPT_FACE",FACE,{"disambiguationData":[OSD([sQuery(id+"F7.wireOp",EDGE,"E17.right")])]})])],"derivedFrom":makeQuery(id+"F1.opExtrude","SWEPT_FACE",FACE,{"disambiguationData":[OSD([subQ1])]})}),makeQuery(id+"F13.opExtrude","SWEPT_FACE",FACE,{"disambiguationData":[OSD([sQuery(id+"F12.wireOp",EDGE,"E24.left")])]})]});}
            fillet(context, id + "F22", {"entities" : qUnion([Q0, Q1, Q2, Q3, Q4, Q5, Q6, Q7, Q8, Q9, Q10, Q11]), "radius" : 5.08 * mm, "tangentPropagation" : true, "allowEdgeOverflow" : false});
        }
        {
            var Q0;
            {var subQ14=sQuery(id+"F0.wireOp",EDGE,"E10");var subQ15=sQuery(id+"F0.wireOp",EDGE,"E9");var subQ20=makeQuery(id+"F1.opExtrude","SWEPT_EDGE",EDGE,{"disambiguationData":[OSD([subQ15,subQ14])]});Q0=makeQuery(id+"F11.boolean.opBoolean","MERGE",EDGE,{"derivedFrom":[makeQuery(id+"F9.opBoolean","SPLIT",EDGE,{"disambiguationData":[TD([makeQuery(id+"F8.opExtrude","SWEPT_FACE",FACE,{"disambiguationData":[OSD([sQuery(id+"F7.wireOp",EDGE,"E17.left")])]})])],"derivedFrom":subQ20}),makeQuery(id+"F9.opBoolean","SPLIT",EDGE,{"disambiguationData":[TD([makeQuery(id+"F8.opExtrude","SWEPT_FACE",FACE,{"disambiguationData":[OSD([sQuery(id+"F7.wireOp",EDGE,"E17.right")])]})])],"derivedFrom":subQ20}),makeQuery(id+"F11.opExtrude","SWEPT_EDGE",EDGE,{"disambiguationData":[OSD([sQuery(id+"F10.wireOp",EDGE,"E18.5"),sQuery(id+"F10.wireOp",EDGE,"E18.6")])]})]});}
            fillet(context, id + "F23", {"entities" : qUnion([Q0]), "radius" : 5.08 * mm, "tangentPropagation" : true, "allowEdgeOverflow" : false});
        }
        {
            var Q0;
            {var subQ0=sQuery(id+"F0.wireOp",EDGE,"E16.5");var subQ1=sQuery(id+"F0.wireOp",EDGE,"E16.2");Q0=makeQuery(id+"F9.opBoolean","SPLIT",EDGE,{"disambiguationData":[TD([makeQuery(id+"F8.opExtrude","SWEPT_FACE",FACE,{"disambiguationData":[OSD([sQuery(id+"F7.wireOp",EDGE,"E17.right")])]})])],"derivedFrom":makeQuery(id+"F1.opExtrude","SWEPT_EDGE",EDGE,{"disambiguationData":[OSD([subQ1,subQ0])]})});}
            var Q1;
            {var subQ0=sQuery(id+"F0.wireOp",EDGE,"E16.5");var subQ1=sQuery(id+"F0.wireOp",EDGE,"E16.2");Q1=makeQuery(id+"F9.opBoolean","SPLIT",EDGE,{"disambiguationData":[TD([makeQuery(id+"F8.opExtrude","SWEPT_FACE",FACE,{"disambiguationData":[OSD([sQuery(id+"F7.wireOp",EDGE,"E17.left")])]})])],"derivedFrom":makeQuery(id+"F1.opExtrude","SWEPT_EDGE",EDGE,{"disambiguationData":[OSD([subQ1,subQ0])]})});}
            fillet(context, id + "F24", {"entities" : qUnion([Q0, Q1]), "radius" : 5.08 * mm, "tangentPropagation" : true, "allowEdgeOverflow" : false});
        }
        {
            var Q0;
            {var subQ0=sQuery(id+"F0.wireOp",EDGE,"E16.4");var subQ1=sQuery(id+"F0.wireOp",EDGE,"E16.3");Q0=makeQuery(id+"F9.opBoolean","SPLIT",EDGE,{"disambiguationData":[TD([makeQuery(id+"F8.opExtrude","SWEPT_FACE",FACE,{"disambiguationData":[OSD([sQuery(id+"F7.wireOp",EDGE,"E17.left")])]})])],"derivedFrom":makeQuery(id+"F1.opExtrude","SWEPT_EDGE",EDGE,{"disambiguationData":[OSD([subQ1,subQ0])]})});}
            var Q1;
            {var subQ0=sQuery(id+"F0.wireOp",EDGE,"E16.2");var subQ1=sQuery(id+"F0.wireOp",EDGE,"E16.0");Q1=makeQuery(id+"F9.opBoolean","SPLIT",EDGE,{"disambiguationData":[TD([makeQuery(id+"F8.opExtrude","SWEPT_FACE",FACE,{"disambiguationData":[OSD([sQuery(id+"F7.wireOp",EDGE,"E17.left")])]})])],"derivedFrom":makeQuery(id+"F1.opExtrude","SWEPT_EDGE",EDGE,{"disambiguationData":[OSD([subQ1,subQ0])]})});}
            var Q2;
            {var subQ0=sQuery(id+"F0.wireOp",EDGE,"E16.4");var subQ1=sQuery(id+"F0.wireOp",EDGE,"E16.3");Q2=makeQuery(id+"F9.opBoolean","SPLIT",EDGE,{"disambiguationData":[TD([makeQuery(id+"F8.opExtrude","SWEPT_FACE",FACE,{"disambiguationData":[OSD([sQuery(id+"F7.wireOp",EDGE,"E17.right")])]})])],"derivedFrom":makeQuery(id+"F1.opExtrude","SWEPT_EDGE",EDGE,{"disambiguationData":[OSD([subQ1,subQ0])]})});}
            var Q3;
            {var subQ0=sQuery(id+"F0.wireOp",EDGE,"E16.2");var subQ1=sQuery(id+"F0.wireOp",EDGE,"E16.0");Q3=makeQuery(id+"F9.opBoolean","SPLIT",EDGE,{"disambiguationData":[TD([makeQuery(id+"F8.opExtrude","SWEPT_FACE",FACE,{"disambiguationData":[OSD([sQuery(id+"F7.wireOp",EDGE,"E17.right")])]})])],"derivedFrom":makeQuery(id+"F1.opExtrude","SWEPT_EDGE",EDGE,{"disambiguationData":[OSD([subQ1,subQ0])]})});}
            fillet(context, id + "F25", {"entities" : qUnion([Q0, Q1, Q2, Q3]), "radius" : 5.08 * mm, "tangentPropagation" : true, "allowEdgeOverflow" : false});
        }
        {
            var Q0;
            {var subQ11=sQuery(id+"F0.wireOp",EDGE,"E0");var subQ14=makeQuery(id+"F1.opExtrude","SWEPT_FACE",FACE,{"disambiguationData":[OSD([subQ11])]});Q0=makeQuery(id+"F11.boolean.opBoolean","MERGE",FACE,{"derivedFrom":[makeQuery(id+"F9.opBoolean","SPLIT",FACE,{"disambiguationData":[TD([makeQuery(id+"F8.opExtrude","SWEPT_FACE",FACE,{"disambiguationData":[OSD([sQuery(id+"F7.wireOp",EDGE,"E17.left")])]})])],"derivedFrom":subQ14}),makeQuery(id+"F9.opBoolean","SPLIT",FACE,{"disambiguationData":[TD([makeQuery(id+"F8.opExtrude","SWEPT_FACE",FACE,{"disambiguationData":[OSD([sQuery(id+"F7.wireOp",EDGE,"E17.right")])]})])],"derivedFrom":subQ14}),makeQuery(id+"F11.opExtrude","SWEPT_FACE",FACE,{"disambiguationData":[OSD([sQuery(id+"F10.wireOp",EDGE,"E19.3")])]})]});}
            var sketch = newSketch(context, id + "F26", { "sketchPlane" : qUnion([Q0])});
            skCircle(sketch, "E33.0", {"center": v(236.83, 17.46) * mm, "radius": 4.76 * mm});
            skSolve(sketch);
        }
        {
            var Q0;
            Q0 = qSketchRegion(id + "F26", true);
            extrude(context, id + "F27", {"entities" : qUnion([Q0]), "operationType" : NewBodyOperationType.REMOVE, "oppositeDirection" : true, "depth" : 1.27 * mm});
        }
        {
            var Q0;
            {var subQ3=makeQuery(id+"F1.opExtrude","SWEPT_FACE",FACE,{"disambiguationData":[OSD([sQuery(id+"F0.wireOp",EDGE,"E16.0")])]});Q0=makeQuery(id+"F14.opBoolean","SPLIT",FACE,{"disambiguationData":[TD([subQ3])],"derivedFrom":makeQuery(id+"F9.opBoolean","SPLIT",FACE,{"disambiguationData":[TD([subQ3])],"derivedFrom":makeQuery(id+"F8.opExtrude","SWEPT_FACE",FACE,{"disambiguationData":[OSD([sQuery(id+"F7.wireOp",EDGE,"E17.left")])]})})});}
            var Q1;
            {var subQ1=makeQuery(id+"F1.opExtrude","SWEPT_FACE",FACE,{"disambiguationData":[OSD([sQuery(id+"F0.wireOp",EDGE,"E16.6")])]});Q1=makeQuery(id+"F14.opBoolean","SPLIT",FACE,{"disambiguationData":[TD([subQ1])],"derivedFrom":makeQuery(id+"F9.opBoolean","SPLIT",FACE,{"disambiguationData":[TD([makeQuery(id+"F1.opExtrude","SWEPT_FACE",FACE,{"disambiguationData":[OSD([sQuery(id+"F0.wireOp",EDGE,"E16.0")])]})])],"derivedFrom":makeQuery(id+"F8.opExtrude","SWEPT_FACE",FACE,{"disambiguationData":[OSD([sQuery(id+"F7.wireOp",EDGE,"E17.left")])]})})});}
            var Q2;
            {var subQ1=makeQuery(id+"F1.opExtrude","SWEPT_FACE",FACE,{"disambiguationData":[OSD([sQuery(id+"F0.wireOp",EDGE,"E16.6")])]});Q2=makeQuery(id+"F14.opBoolean","SPLIT",FACE,{"disambiguationData":[TD([subQ1])],"derivedFrom":makeQuery(id+"F9.opBoolean","SPLIT",FACE,{"disambiguationData":[TD([makeQuery(id+"F1.opExtrude","SWEPT_FACE",FACE,{"disambiguationData":[OSD([sQuery(id+"F0.wireOp",EDGE,"E16.0")])]})])],"derivedFrom":makeQuery(id+"F8.opExtrude","SWEPT_FACE",FACE,{"disambiguationData":[OSD([sQuery(id+"F7.wireOp",EDGE,"E17.right")])]})})});}
            var Q3;
            {var subQ3=makeQuery(id+"F1.opExtrude","SWEPT_FACE",FACE,{"disambiguationData":[OSD([sQuery(id+"F0.wireOp",EDGE,"E16.0")])]});Q3=makeQuery(id+"F14.opBoolean","SPLIT",FACE,{"disambiguationData":[TD([subQ3])],"derivedFrom":makeQuery(id+"F9.opBoolean","SPLIT",FACE,{"disambiguationData":[TD([subQ3])],"derivedFrom":makeQuery(id+"F8.opExtrude","SWEPT_FACE",FACE,{"disambiguationData":[OSD([sQuery(id+"F7.wireOp",EDGE,"E17.right")])]})})});}
            fillet(context, id + "F28", {"entities" : qUnion([Q0, Q1, Q2, Q3]), "radius" : 1.27 * mm, "tangentPropagation" : true, "allowEdgeOverflow" : false});
        }
        {
            var Q0;
            {var subQ0=sQuery(id+"F0.wireOp",EDGE,"E7");var subQ1=makeQuery(id+"F1.opExtrude","SWEPT_FACE",FACE,{"disambiguationData":[OSD([subQ0])]});var subQ9=sQuery(id+"F0.wireOp",EDGE,"E14");var subQ15=sQuery(id+"F0.wireOp",EDGE,"E8");var subQ17=makeQuery(id+"F3.opFillet","BLEND_EDGE",EDGE,{"blendedFrom":[makeQuery(id+"F1.opExtrude","SWEPT_EDGE",EDGE,{"disambiguationData":[OSD([subQ15,subQ9])]}),subQ1],"blendedInto":[subQ1]});Q0=makeQuery(id+"F11.boolean.opBoolean","MERGE",EDGE,{"derivedFrom":[makeQuery(id+"F9.opBoolean","SPLIT",EDGE,{"disambiguationData":[TD([makeQuery(id+"F8.opExtrude","SWEPT_FACE",FACE,{"disambiguationData":[OSD([sQuery(id+"F7.wireOp",EDGE,"E17.left")])]})])],"derivedFrom":subQ17}),makeQuery(id+"F9.opBoolean","SPLIT",EDGE,{"disambiguationData":[TD([makeQuery(id+"F8.opExtrude","SWEPT_FACE",FACE,{"disambiguationData":[OSD([sQuery(id+"F7.wireOp",EDGE,"E17.right")])]})])],"derivedFrom":subQ17}),makeQuery(id+"F11.opExtrude","SWEPT_EDGE",EDGE,{"disambiguationData":[OSD([sQuery(id+"F10.wireOp",EDGE,"E23.0"),sQuery(id+"F10.wireOp",EDGE,"E23.1")])]})]});}
            fillet(context, id + "F29", {"entities" : qUnion([Q0]), "radius" : 0.64 * mm, "tangentPropagation" : true, "allowEdgeOverflow" : false});
        }
    });
